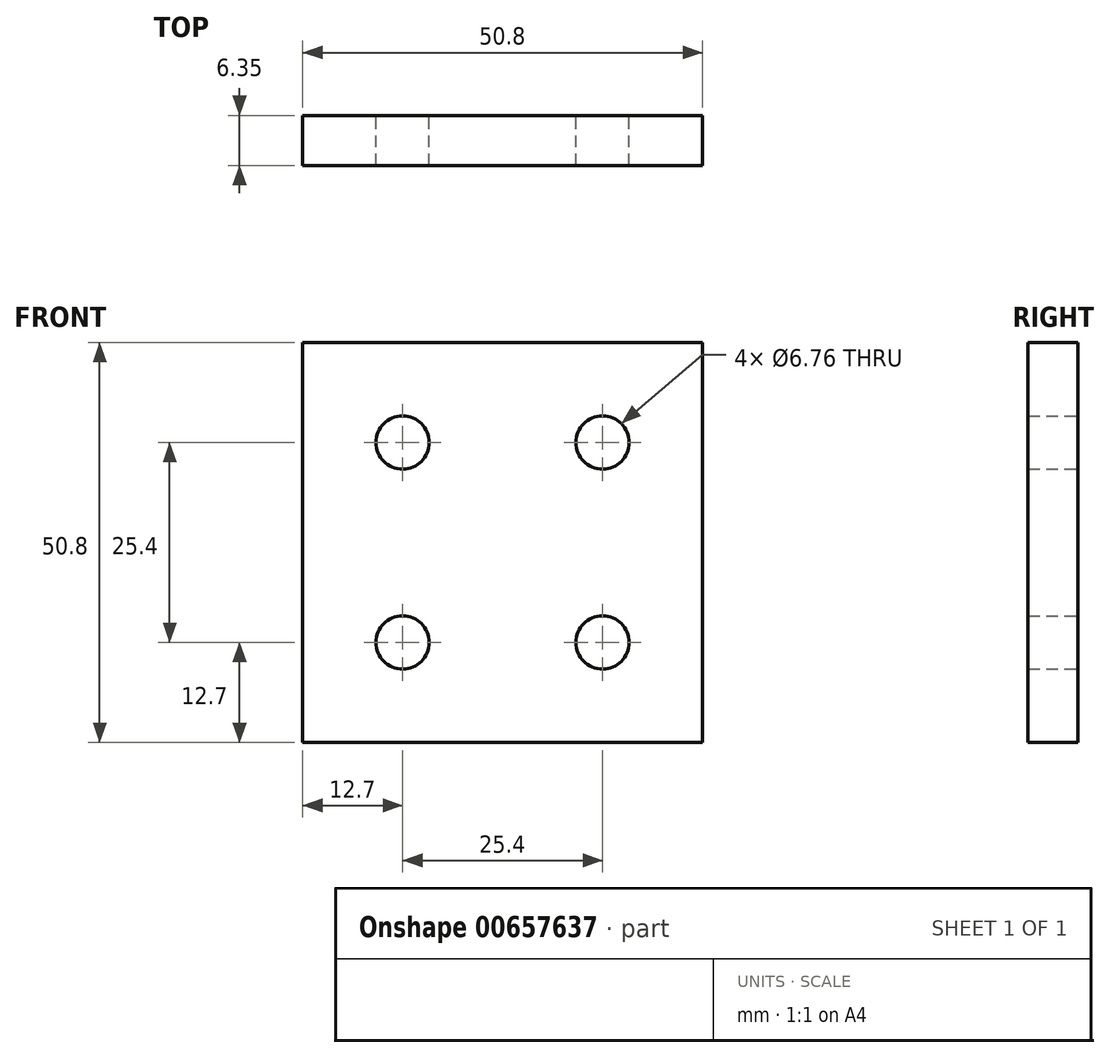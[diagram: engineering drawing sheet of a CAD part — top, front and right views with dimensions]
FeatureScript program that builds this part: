
annotation { "Feature Type Name" : "Feature", "Feature Type Description" : "" }
export const myFeature = defineFeature(function(context is Context, id is Id, definition is map)
    precondition{}
    {
        {
            var Q0;
            Q0=qCreatedBy(makeId("Front.planeOp"),FACE);
            var sketch = newSketch(context, id + "F0", { "sketchPlane" : qUnion([Q0])});
            skLineSegment(sketch, "E0.bottom", {"start": v(0, 0) * mm, "end": v(50.8, 0) * mm});
            skLineSegment(sketch, "E0.top", {"start": v(0, 50.8) * mm, "end": v(50.8, 50.8) * mm});
            skLineSegment(sketch, "E0.left", {"start": v(0, 0) * mm, "end": v(0, 50.8) * mm});
            skLineSegment(sketch, "E0.right", {"start": v(50.8, 0) * mm, "end": v(50.8, 50.8) * mm});
            skCircle(sketch, "E1", {"center": v(12.7, 38.1) * mm, "radius": 3.38 * mm});
            skCircle(sketch, "E2.0.1.0", {"center": v(12.7, 12.7) * mm, "radius": 3.38 * mm});
            skCircle(sketch, "E2.1.0.0", {"center": v(38.1, 38.1) * mm, "radius": 3.38 * mm});
            skCircle(sketch, "E2.1.1.0", {"center": v(38.1, 12.7) * mm, "radius": 3.38 * mm});
            skLineSegment(sketch, "E2.direction1", {"start": v(12.7, 38.1) * mm, "end": v(38.1, 38.1) * mm, "construction": true});
            skLineSegment(sketch, "E2.direction2", {"start": v(12.7, 38.1) * mm, "end": v(12.7, 12.7) * mm, "construction": true});
            skSolve(sketch);
        }
        {
            var Q0;
            Q0=makeQuery(id+"F0.imprint","IMPRINT",FACE,{"disambiguationData":[TD([[makeQuery(id+"F0.imprint","IMPRINT",EDGE,{"derivedFrom":sQuery(id+"F0.wireOp",EDGE,"E0.bottom")}),1.0]])]});
            extrude(context, id + "F1", {"entities" : qUnion([Q0]), "depth" : 6.35 * mm, "offsetDistance" : 25.4 * mm});
        }
    });
